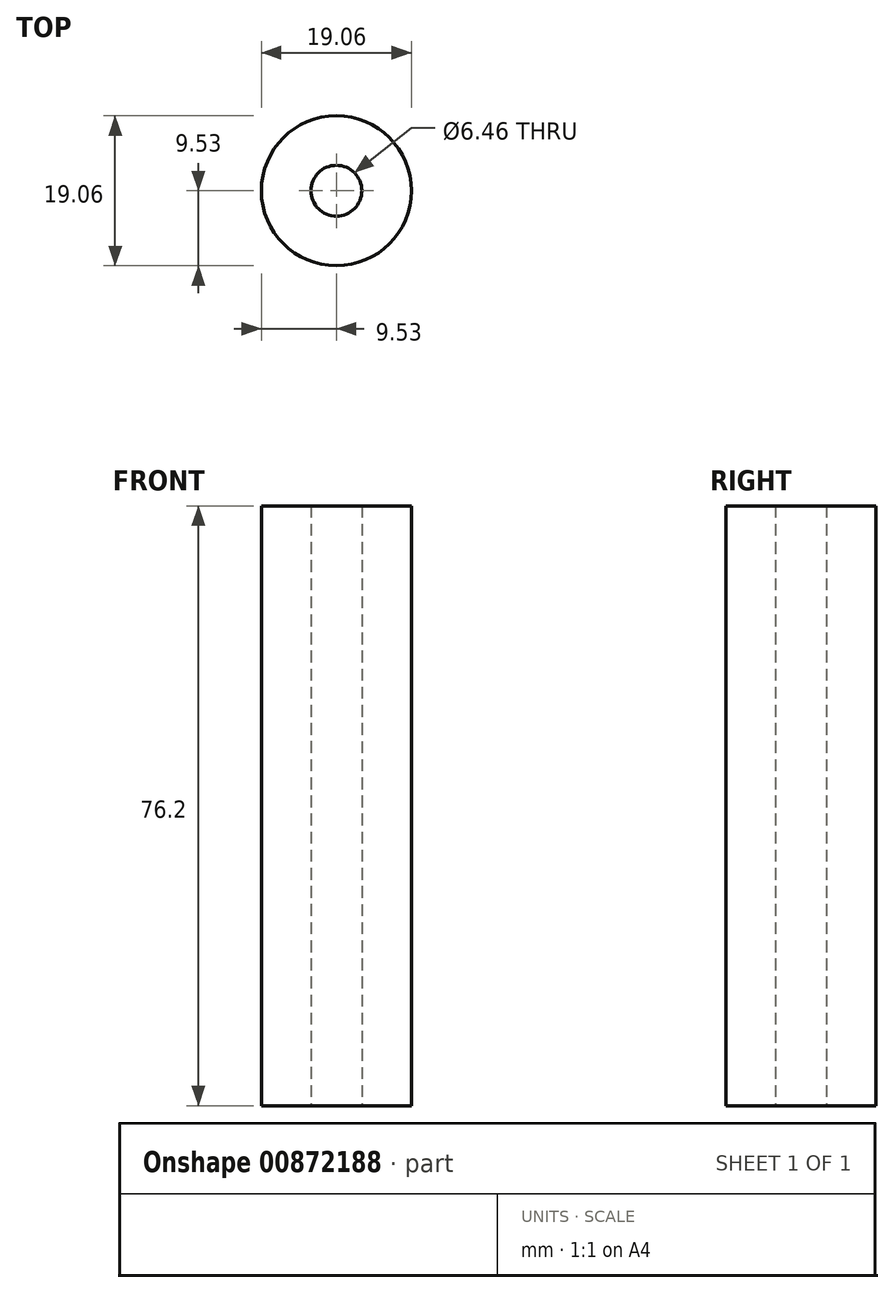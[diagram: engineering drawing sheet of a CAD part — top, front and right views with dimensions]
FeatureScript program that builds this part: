
annotation { "Feature Type Name" : "Feature", "Feature Type Description" : "" }
export const myFeature = defineFeature(function(context is Context, id is Id, definition is map)
    precondition{}
    {
        {
            var Q0;
            Q0=qCreatedBy(makeId("Top.planeOp"),FACE);
            var sketch = newSketch(context, id + "F0", { "sketchPlane" : qUnion([Q0])});
            skCircle(sketch, "E0", {"center": v(0, 0) * mm, "radius": 9.53 * mm});
            skCircle(sketch, "E1", {"center": v(0, 0) * mm, "radius": 3.23 * mm});
            skSolve(sketch);
        }
        {
            var Q0;
            Q0=qSketchRegion(id+"F0",true);
            extrude(context, id + "F1", {"entities" : qUnion([Q0]), "depth" : 76.2 * mm, "offsetDistance" : 25.4 * mm});
        }
    });
